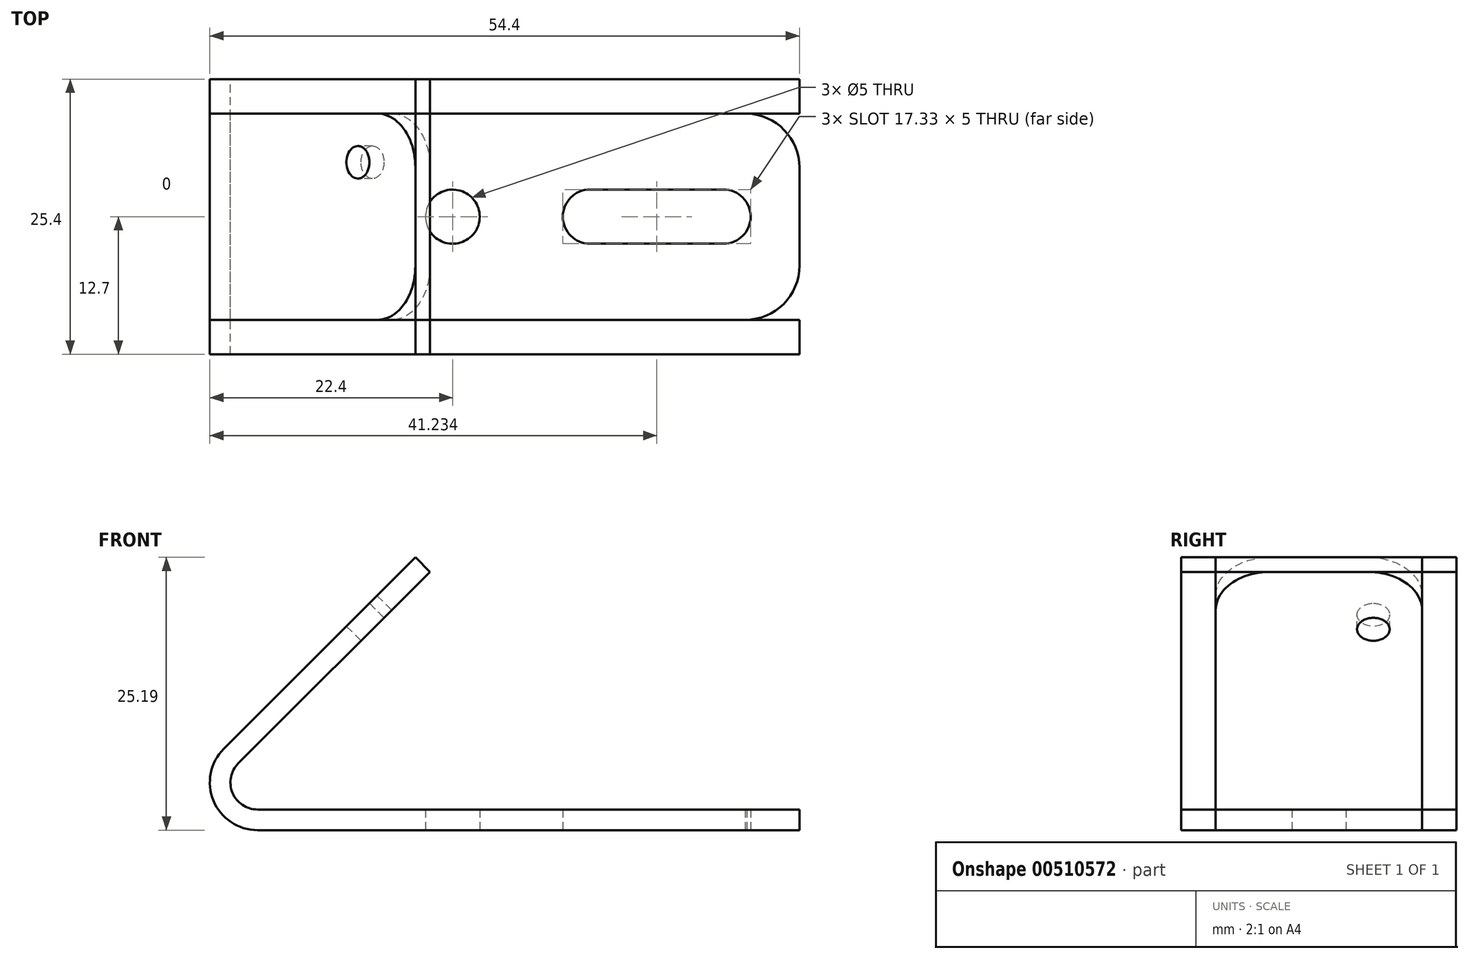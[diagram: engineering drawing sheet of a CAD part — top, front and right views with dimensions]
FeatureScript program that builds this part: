
annotation { "Feature Type Name" : "Feature", "Feature Type Description" : "" }
export const myFeature = defineFeature(function(context is Context, id is Id, definition is map)
    precondition{}
    {
        {
            var Q0;
            Q0=qCreatedBy(makeId("Front.planeOp"),FACE);
            var sketch = newSketch(context, id + "F0", { "sketchPlane" : qUnion([Q0])});
            skArc(sketch, "E0", {"start": v(-3.11, 7.51) * mm, "mid": v(-4.07, 2.72) * mm, "end": v(0, 0) * mm});
            skArc(sketch, "E1", {"start": v(-1.77, 6.17) * mm, "mid": v(-2.3, 3.44) * mm, "end": v(0, 1.9) * mm});
            skLineSegment(sketch, "E2.bottom", {"start": v(0, 0) * mm, "end": v(50, 0) * mm});
            skLineSegment(sketch, "E2.top", {"start": v(0, 1.9) * mm, "end": v(50, 1.9) * mm});
            skLineSegment(sketch, "E2.right", {"start": v(50, 0) * mm, "end": v(50, 1.9) * mm});
            skLineSegment(sketch, "E3", {"start": v(-3.11, 7.51) * mm, "end": v(14.57, 25.19) * mm});
            skLineSegment(sketch, "E4", {"start": v(14.57, 25.19) * mm, "end": v(15.9, 23.85) * mm});
            skLineSegment(sketch, "E5", {"start": v(15.9, 23.85) * mm, "end": v(-1.77, 6.17) * mm});
            skSolve(sketch);
        }
        {
            var Q0;
            Q0=qCreatedBy(makeId("Top.planeOp"),FACE);
            var sketch = newSketch(context, id + "F1", { "sketchPlane" : qUnion([Q0])});
            skLineSegment(sketch, "E6.bottom", {"start": v(45, 9.52) * mm, "end": v(0, 9.52) * mm, "construction": true});
            skLineSegment(sketch, "E6.top", {"start": v(45, -9.53) * mm, "end": v(0, -9.53) * mm, "construction": true});
            skLineSegment(sketch, "E6.left", {"start": v(50, 4.53) * mm, "end": v(50, -4.52) * mm, "construction": true});
            skLineSegment(sketch, "E6.right", {"start": v(0, 9.52) * mm, "end": v(0, -9.53) * mm});
            skPoint(sketch, "E6.middle", {"position": v(25, 0) * mm});
            skCircle(sketch, "E7", {"center": v(18, 0) * mm, "radius": 2.5 * mm});
            skPoint(sketch, "E7.centerSnap0", {"position": v(0, 0) * mm});
            skArc(sketch, "E8", {"start": v(30.67, 2.5) * mm, "mid": v(28.9, 1.77) * mm, "end": v(28.17, 0) * mm});
            skArc(sketch, "E9", {"start": v(43, -2.5) * mm, "mid": v(44.77, -1.77) * mm, "end": v(45.5, 0) * mm});
            skLineSegment(sketch, "E10", {"start": v(30.67, 2.5) * mm, "end": v(43, 2.5) * mm});
            skLineSegment(sketch, "E11", {"start": v(30.67, -2.5) * mm, "end": v(43, -2.5) * mm});
            skArc(sketch, "E12", {"start": v(28.17, 0) * mm, "mid": v(28.9, -1.77) * mm, "end": v(30.67, -2.5) * mm});
            skArc(sketch, "E13", {"start": v(45.5, 0) * mm, "mid": v(44.77, 1.77) * mm, "end": v(43, 2.5) * mm});
            skPoint(sketch, "E14.visualSharp", {"position": v(50, 9.52) * mm});
            skArc(sketch, "E14.filletArc", {"start": v(50, 4.53) * mm, "mid": v(48.54, 8.06) * mm, "end": v(45, 9.53) * mm});
            skPoint(sketch, "E15.visualSharp", {"position": v(50, -9.53) * mm});
            skArc(sketch, "E15.filletArc", {"start": v(45, -9.52) * mm, "mid": v(48.54, -8.06) * mm, "end": v(50, -4.52) * mm});
            skLineSegment(sketch, "E16", {"start": v(50, 4.53) * mm, "end": v(50, 9.52) * mm});
            skLineSegment(sketch, "E17", {"start": v(45.17, 9.52) * mm, "end": v(50, 9.52) * mm});
            skLineSegment(sketch, "E18", {"start": v(50, -4.52) * mm, "end": v(50, -9.53) * mm});
            skLineSegment(sketch, "E19", {"start": v(45, -9.53) * mm, "end": v(50, -9.53) * mm});
            skSolve(sketch);
        }
        {
            var Q0;
            Q0=sQuery(id+"F0.wireOp",EDGE,"E3");
            cPlane(context, id + "F2", {"entities" : qUnion([Q0]), "cplaneType" : CPlaneType.LINE_ANGLE, "offset" : 25 * mm, "angle" : 90 * degree, "width" : 150 * mm, "height" : 150 * mm});
        }
        {
            var Q0;
            Q0=qCreatedBy(id+"F2.planeOp",FACE);
            var sketch = newSketch(context, id + "F3", { "sketchPlane" : qUnion([Q0])});
            skPoint(sketch, "E20.0", {"position": v(-9.52, 15.9) * mm});
            skLineSegment(sketch, "E21.bottom", {"start": v(-9.52, 28.11) * mm, "end": v(-4.53, 28.11) * mm});
            skLineSegment(sketch, "E21.left", {"start": v(-9.52, 28.11) * mm, "end": v(-9.52, 23.11) * mm});
            skLineSegment(sketch, "E21.right", {"start": v(9.52, 28.11) * mm, "end": v(9.52, 23.11) * mm});
            skPoint(sketch, "E21.middle", {"position": v(0, 15.61) * mm});
            skPoint(sketch, "E22.visualSharp", {"position": v(-9.52, 28.11) * mm});
            skArc(sketch, "E22.filletArc", {"start": v(-4.53, 28.11) * mm, "mid": v(-8.06, 26.65) * mm, "end": v(-9.52, 23.11) * mm});
            skPoint(sketch, "E23.visualSharp", {"position": v(9.52, 28.11) * mm});
            skArc(sketch, "E23.filletArc", {"start": v(9.52, 23.11) * mm, "mid": v(8.06, 26.65) * mm, "end": v(4.52, 28.11) * mm});
            skLineSegment(sketch, "E24", {"start": v(4.52, 23.11) * mm, "end": v(4.52, 35.36) * mm, "construction": true});
            skLineSegment(sketch, "E25", {"start": v(-4.53, 23.11) * mm, "end": v(-4.53, 35.36) * mm, "construction": true});
            skCircle(sketch, "E26", {"center": v(-5.02, 20.61) * mm, "radius": 1.5 * mm});
            skCircle(sketch, "E27.MirrorC", {"center": v(5.02, 20.61) * mm, "radius": 1.5 * mm});
            skPoint(sketch, "E21.top.start.orphan", {"position": v(-9.52, 3.11) * mm});
            skPoint(sketch, "E28.orphan", {"position": v(9.53, 3.11) * mm});
            skLineSegment(sketch, "E29.trimOffspring", {"start": v(4.52, 28.11) * mm, "end": v(9.52, 28.11) * mm});
            skLineSegment(sketch, "E30", {"start": v(-4.53, 28.11) * mm, "end": v(0, 28.11) * mm, "construction": true});
            skLineSegment(sketch, "E31", {"start": v(0, 28.11) * mm, "end": v(4.52, 28.11) * mm, "construction": true});
            skSolve(sketch);
        }
        {
            var Q0;
            Q0=makeQuery(id+"F0.imprint","IMPRINT",FACE,{"disambiguationData":[TD([[makeQuery(id+"F0.imprint","IMPRINT",EDGE,{"derivedFrom":sQuery(id+"F0.wireOp",EDGE,"E0")}),1.0]])]});
            var Q1;
            Q1=sQuery(id+"F3.wireOp",VERTEX,"E23.visualSharp");
            var Q2;
            Q2=sQuery(id+"F3.wireOp",VERTEX,"E22.visualSharp");
            extrude(context, id + "F4", {"entities" : qUnion([Q0]), "endBound" : BoundingType.UP_TO_VERTEX, "depth" : 25.4 * mm, "endBoundEntityVertex" : qUnion([Q1]), "offsetDistance" : 25.4 * mm, "hasSecondDirection" : true, "secondDirectionBound" : SecondDirectionBoundingType.UP_TO_VERTEX, "secondDirectionOppositeDirection" : true, "secondDirectionDepth" : 25.4 * mm, "secondDirectionBoundEntityVertex" : qUnion([Q2])});
        }
        {
            var Q0;
            Q0=makeQuery(id+"F0.imprint","IMPRINT",FACE,{"disambiguationData":[TD([[makeQuery(id+"F0.imprint","IMPRINT",EDGE,{"derivedFrom":sQuery(id+"F0.wireOp",EDGE,"E0")}),1.0]])]});
            extrude(context, id + "F5", {"entities" : qUnion([Q0]), "endBound" : BoundingType.SYMMETRIC, "depth" : 25.4 * mm, "hasSecondDirection" : true, "secondDirectionOppositeDirection" : true, "secondDirectionDepth" : 25.4 * mm});
        }
        {
            var Q0;
            Q0=makeQuery(id+"F3.imprint","IMPRINT",FACE,{"disambiguationData":[TD([[makeQuery(id+"F3.imprint","IMPRINT",EDGE,{"derivedFrom":sQuery(id+"F3.wireOp",EDGE,"E27.MirrorC")}),-1.0]])]});
            var Q1;
            Q1=makeQuery(id+"F3.imprint","IMPRINT",FACE,{"disambiguationData":[TD([[makeQuery(id+"F3.imprint","IMPRINT",EDGE,{"derivedFrom":sQuery(id+"F3.wireOp",EDGE,"E26")}),1.0]])]});
            var Q2;
            Q2=makeQuery(id+"F3.imprint","IMPRINT",FACE,{"disambiguationData":[TD([[makeQuery(id+"F3.imprint","IMPRINT",EDGE,{"derivedFrom":sQuery(id+"F3.wireOp",EDGE,"E21.right")}),-1.0]])]});
            var Q3;
            Q3=makeQuery(id+"F3.imprint","IMPRINT",FACE,{"disambiguationData":[TD([[makeQuery(id+"F3.imprint","IMPRINT",EDGE,{"derivedFrom":sQuery(id+"F3.wireOp",EDGE,"E21.bottom")}),-1.0]])]});
            extrude(context, id + "F6", {"entities" : qUnion([Q0, Q1, Q2, Q3]), "operationType" : NewBodyOperationType.REMOVE, "endBound" : BoundingType.UP_TO_NEXT, "oppositeDirection" : true, "depth" : 25.4 * mm, "offsetDistance" : 25.4 * mm});
        }
        {
            var Q0;
            Q0=makeQuery(id+"F1.imprint","IMPRINT",FACE,{"disambiguationData":[TD([[makeQuery(id+"F1.imprint","IMPRINT",EDGE,{"derivedFrom":sQuery(id+"F1.wireOp",EDGE,"E7")}),1.0]])]});
            var Q1;
            Q1=makeQuery(id+"F1.imprint","IMPRINT",FACE,{"disambiguationData":[TD([[makeQuery(id+"F1.imprint","IMPRINT",EDGE,{"derivedFrom":sQuery(id+"F1.wireOp",EDGE,"E8")}),1.0]])]});
            var Q2;
            Q2=makeQuery(id+"F1.imprint","IMPRINT",FACE,{"disambiguationData":[TD([[makeQuery(id+"F1.imprint","IMPRINT",EDGE,{"derivedFrom":sQuery(id+"F1.wireOp",EDGE,"E15.filletArc")}),-1.0]])]});
            var Q3;
            {var subQ0=sQuery(id+"F1.wireOp",EDGE,"E16");Q3=makeQuery(id+"F1.imprint","IMPRINT",FACE,{"disambiguationData":[TD([[makeQuery(id+"F1.imprint","IMPRINT",EDGE,{"derivedFrom":subQ0}),1.0]])]});}
            extrude(context, id + "F7", {"entities" : qUnion([Q0, Q1, Q2, Q3]), "operationType" : NewBodyOperationType.REMOVE, "endBound" : BoundingType.UP_TO_NEXT, "depth" : 25.4 * mm, "offsetDistance" : 25.4 * mm});
        }
        {
            var Q0;
            Q0=makeQuery(id+"F0.imprint","IMPRINT",FACE,{"disambiguationData":[TD([[makeQuery(id+"F0.imprint","IMPRINT",EDGE,{"derivedFrom":sQuery(id+"F0.wireOp",EDGE,"E0")}),1.0]])]});
            var Q1;
            Q1=sQuery(id+"F1.wireOp",VERTEX,"E6.right.end");
            var Q2;
            Q2=sQuery(id+"F1.wireOp",VERTEX,"E6.right.start");
            extrude(context, id + "F8", {"entities" : qUnion([Q0]), "endBound" : BoundingType.UP_TO_VERTEX, "endBoundEntityVertex" : qUnion([Q1]), "depth" : 25 * mm, "hasSecondDirection" : true, "secondDirectionBound" : SecondDirectionBoundingType.UP_TO_VERTEX, "secondDirectionOppositeDirection" : true, "secondDirectionBoundEntityVertex" : qUnion([Q2]), "secondDirectionDepth" : 25 * mm});
        }
        {
            var Q0;
            Q0=qSketchRegion(id+"F1",true);
            var Q1;
            Q1=sQuery(id+"F0.wireOp",VERTEX,"E2.right.end");
            extrude(context, id + "F9", {"entities" : qUnion([Q0]), "operationType" : NewBodyOperationType.REMOVE, "endBound" : BoundingType.UP_TO_VERTEX, "endBoundEntityVertex" : qUnion([Q1]), "depth" : 25 * mm});
        }
    });
